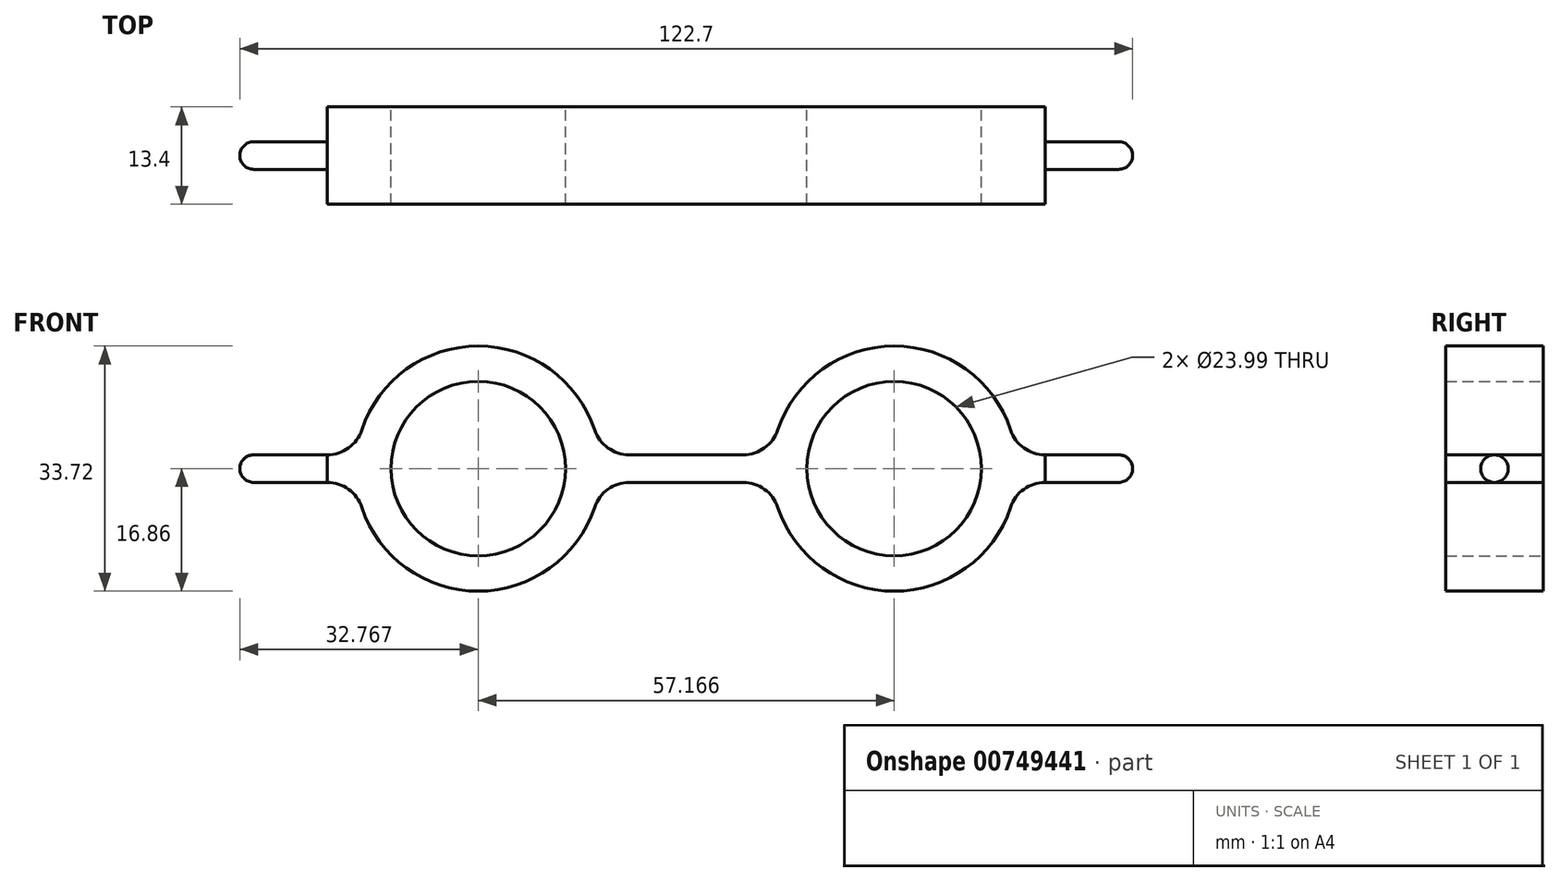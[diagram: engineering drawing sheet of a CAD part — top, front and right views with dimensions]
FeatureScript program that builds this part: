
annotation { "Feature Type Name" : "Feature", "Feature Type Description" : "" }
export const myFeature = defineFeature(function(context is Context, id is Id, definition is map)
    precondition{}
    {
        {
            var Q0;
            Q0=qCreatedBy(makeId("Front.planeOp"),FACE);
            var sketch = newSketch(context, id + "F0", { "sketchPlane" : qUnion([Q0])});
            skCircle(sketch, "E0", {"center": v(-28.58, 0) * mm, "radius": 12 * mm});
            skArc(sketch, "E1", {"start": v(-44.58, -5.32) * mm, "mid": v(-28.58, -16.86) * mm, "end": v(-12.58, -5.32) * mm});
            skLineSegment(sketch, "E2", {"start": v(-7.84, 1.9) * mm, "end": v(0, 1.9) * mm});
            skLineSegment(sketch, "E3.MirrorCS", {"start": v(-7.84, -1.9) * mm, "end": v(0, -1.9) * mm});
            skLineSegment(sketch, "E4", {"start": v(-49.33, 1.9) * mm, "end": v(-59.45, 1.9) * mm});
            skLineSegment(sketch, "E5", {"start": v(-59.45, -1.9) * mm, "end": v(-49.33, -1.9) * mm});
            skArc(sketch, "E6", {"start": v(-59.45, 1.9) * mm, "mid": v(-61.35, 0) * mm, "end": v(-59.45, -1.9) * mm});
            skArc(sketch, "E7.trimOffspring", {"start": v(-12.58, 5.32) * mm, "mid": v(-28.58, 16.86) * mm, "end": v(-44.58, 5.32) * mm});
            skPoint(sketch, "E8.visualSharp", {"position": v(-45.34, 1.9) * mm});
            skArc(sketch, "E8.filletArc", {"start": v(-49.33, 1.9) * mm, "mid": v(-46.4, 2.84) * mm, "end": v(-44.58, 5.32) * mm});
            skPoint(sketch, "E9.visualSharp", {"position": v(-45.34, -1.9) * mm});
            skArc(sketch, "E9.filletArc", {"start": v(-44.58, -5.32) * mm, "mid": v(-46.4, -2.84) * mm, "end": v(-49.33, -1.9) * mm});
            skPoint(sketch, "E10.visualSharp", {"position": v(-11.83, 1.9) * mm});
            skArc(sketch, "E10.filletArc", {"start": v(-12.58, 5.32) * mm, "mid": v(-10.76, 2.84) * mm, "end": v(-7.84, 1.9) * mm});
            skPoint(sketch, "E11.visualSharp", {"position": v(-11.83, -1.9) * mm});
            skArc(sketch, "E11.filletArc", {"start": v(-7.84, -1.9) * mm, "mid": v(-10.76, -2.84) * mm, "end": v(-12.58, -5.32) * mm});
            skArc(sketch, "E12.MirrorCS", {"start": v(44.58, -5.32) * mm, "mid": v(46.4, -2.84) * mm, "end": v(49.33, -1.9) * mm});
            skArc(sketch, "E13.MirrorCS", {"start": v(49.33, 1.9) * mm, "mid": v(46.4, 2.84) * mm, "end": v(44.58, 5.32) * mm});
            skArc(sketch, "E14.MirrorCS", {"start": v(7.84, -1.9) * mm, "mid": v(10.76, -2.84) * mm, "end": v(12.58, -5.32) * mm});
            skArc(sketch, "E15.MirrorCS", {"start": v(12.58, 5.32) * mm, "mid": v(10.76, 2.84) * mm, "end": v(7.84, 1.9) * mm});
            skCircle(sketch, "E16.MirrorC", {"center": v(28.58, 0) * mm, "radius": 12 * mm});
            skPoint(sketch, "E17.MirrorP", {"position": v(11.83, 1.9) * mm});
            skPoint(sketch, "E18.MirrorP", {"position": v(45.34, 1.9) * mm});
            skPoint(sketch, "E19.MirrorP", {"position": v(45.34, -1.9) * mm});
            skArc(sketch, "E20.MirrorCS", {"start": v(44.58, -5.32) * mm, "mid": v(28.58, -16.86) * mm, "end": v(12.58, -5.32) * mm});
            skLineSegment(sketch, "E21.MirrorCS", {"start": v(7.84, -1.9) * mm, "end": v(0, -1.9) * mm});
            skLineSegment(sketch, "E22.MirrorCS", {"start": v(7.84, 1.9) * mm, "end": v(0, 1.9) * mm});
            skArc(sketch, "E23.MirrorCS", {"start": v(12.58, 5.32) * mm, "mid": v(28.58, 16.86) * mm, "end": v(44.58, 5.32) * mm});
            skPoint(sketch, "E24.MirrorP", {"position": v(11.83, -1.9) * mm});
            skArc(sketch, "E25.MirrorCS", {"start": v(59.45, 1.9) * mm, "mid": v(61.35, 0) * mm, "end": v(59.45, -1.9) * mm});
            skLineSegment(sketch, "E26.MirrorCS", {"start": v(59.45, -1.9) * mm, "end": v(49.33, -1.9) * mm});
            skLineSegment(sketch, "E27.MirrorCS", {"start": v(49.33, 1.9) * mm, "end": v(59.45, 1.9) * mm});
            skLineSegment(sketch, "E28", {"start": v(-49.33, 1.9) * mm, "end": v(-49.33, -1.9) * mm});
            skLineSegment(sketch, "E29", {"start": v(49.33, 1.9) * mm, "end": v(49.33, -1.9) * mm});
            skLineSegment(sketch, "E30", {"start": v(-61.35, 0) * mm, "end": v(-49.33, 0) * mm});
            skLineSegment(sketch, "E31", {"start": v(49.33, 0) * mm, "end": v(61.35, 0) * mm});
            skSolve(sketch);
        }
        {
            var Q0;
            Q0=makeQuery(id+"F0.imprint","IMPRINT",FACE,{"disambiguationData":[TD([[makeQuery(id+"F0.imprint","IMPRINT",EDGE,{"derivedFrom":sQuery(id+"F0.wireOp",EDGE,"E0")}),-1.0]])]});
            extrude(context, id + "F1", {"entities" : qUnion([Q0]), "depth" : 6.7 * mm, "offsetDistance" : 25 * mm, "hasSecondDirection" : true, "secondDirectionOppositeDirection" : true, "secondDirectionDepth" : 6.7 * mm});
        }
        {
            var Q0;
            {var subQ0=sQuery(id+"F0.wireOp",EDGE,"E4");Q0=makeQuery(id+"F0.imprint","IMPRINT",FACE,{"disambiguationData":[TD([[makeQuery(id+"F0.imprint","IMPRINT",EDGE,{"derivedFrom":subQ0}),1.0]])]});}
            var Q1;
            Q1=sQuery(id+"F0.wireOp",EDGE,"E30");
            revolve(context, id + "F2", {"operationType" : NewBodyOperationType.ADD, "surfaceOperationType" : NewSurfaceOperationType.NEW, "entities" : qUnion([Q0]), "axis" : qUnion([Q1]), "revolveType" : RevolveType.FULL});
        }
        {
            var Q0;
            {var subQ0=sQuery(id+"F0.wireOp",EDGE,"E27.MirrorCS");Q0=makeQuery(id+"F0.imprint","IMPRINT",FACE,{"disambiguationData":[TD([[makeQuery(id+"F0.imprint","IMPRINT",EDGE,{"derivedFrom":subQ0}),-1.0]])]});}
            var Q1;
            Q1=sQuery(id+"F0.wireOp",EDGE,"E31");
            revolve(context, id + "F3", {"operationType" : NewBodyOperationType.ADD, "surfaceOperationType" : NewSurfaceOperationType.NEW, "entities" : qUnion([Q0]), "axis" : qUnion([Q1]), "revolveType" : RevolveType.FULL});
        }
    });
